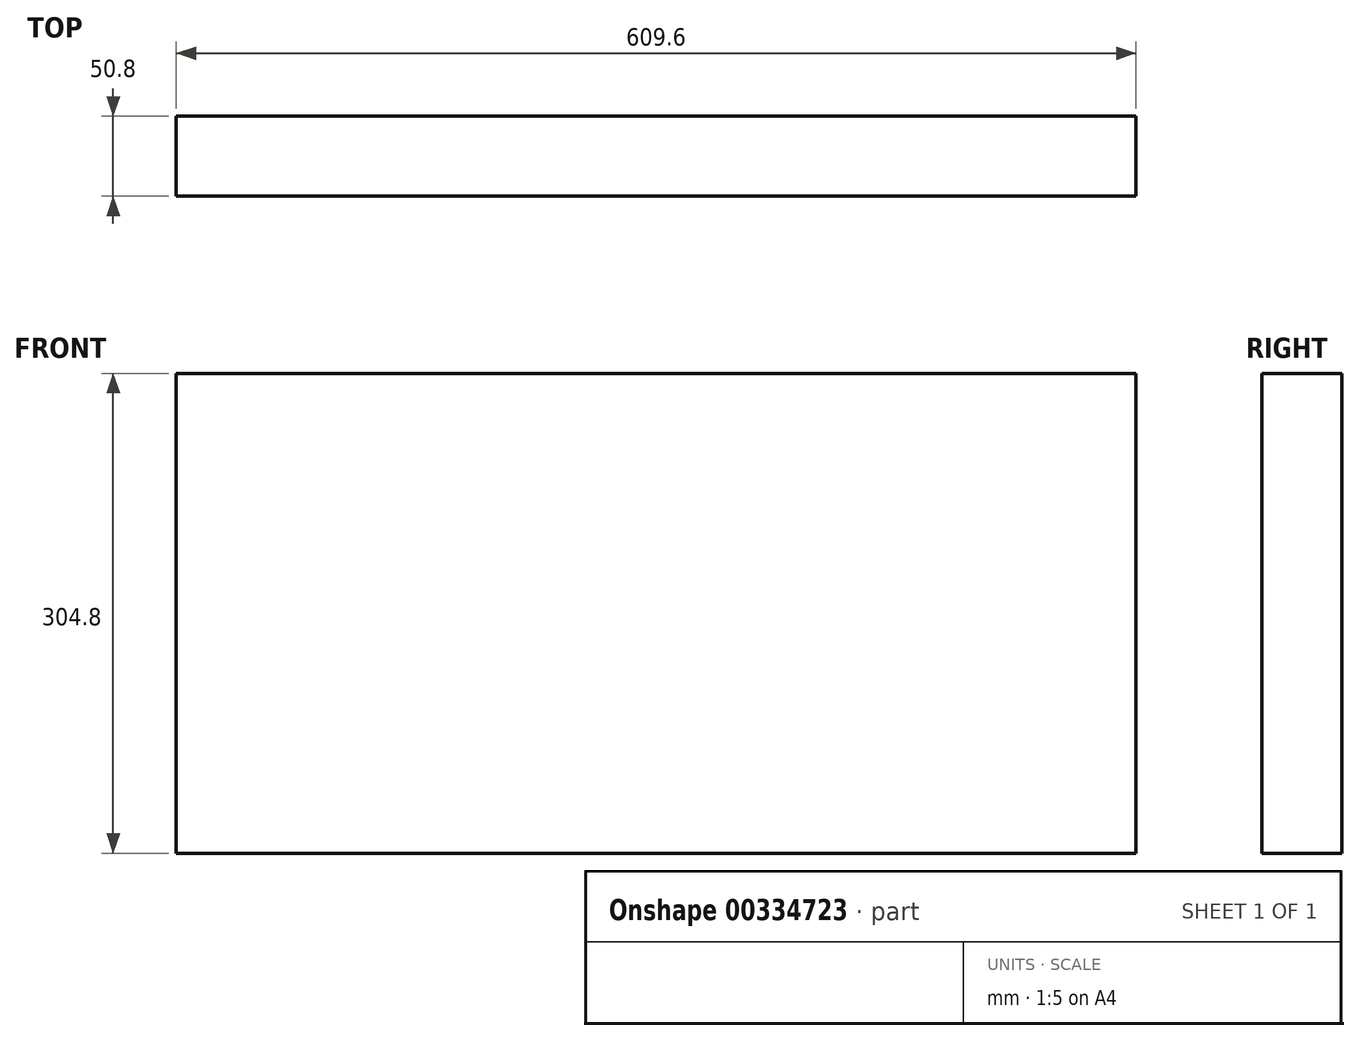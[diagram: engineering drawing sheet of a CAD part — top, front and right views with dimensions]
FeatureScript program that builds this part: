
annotation { "Feature Type Name" : "Feature", "Feature Type Description" : "" }
export const myFeature = defineFeature(function(context is Context, id is Id, definition is map)
    precondition{}
    {
        {
            var Q0;
            Q0=qCreatedBy(makeId("Front.planeOp"),FACE);
            var sketch = newSketch(context, id + "F0", { "sketchPlane" : qUnion([Q0])});
            skLineSegment(sketch, "E0", {"start": v(-291.15, 304.8) * mm, "end": v(318.45, 304.8) * mm});
            skLineSegment(sketch, "E1", {"start": v(318.45, 0) * mm, "end": v(318.45, 304.8) * mm});
            skLineSegment(sketch, "E2", {"start": v(-291.15, 304.8) * mm, "end": v(-291.15, 0) * mm});
            skLineSegment(sketch, "E3", {"start": v(-291.15, 0) * mm, "end": v(318.45, 0) * mm});
            skSolve(sketch);
        }
        {
            var Q0;
            Q0 = qSketchRegion(id + "F0", true);
            extrude(context, id + "F1", {"entities" : qUnion([Q0]), "depth" : 50.8 * mm});
        }
    });
